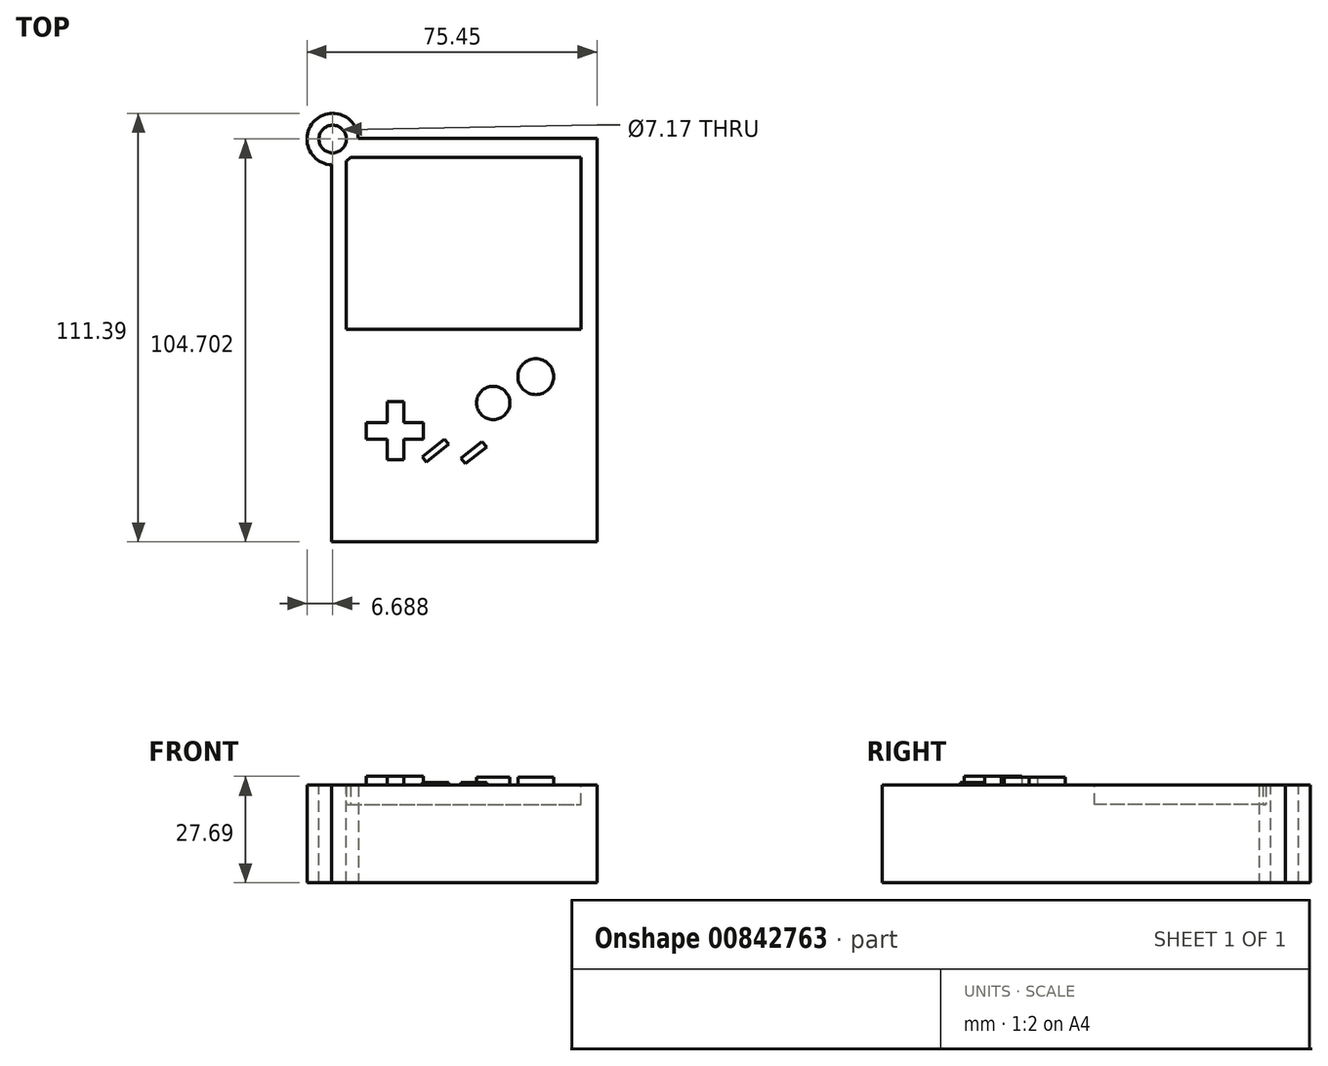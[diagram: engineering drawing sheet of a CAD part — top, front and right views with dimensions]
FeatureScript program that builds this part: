
annotation { "Feature Type Name" : "Feature", "Feature Type Description" : "" }
export const myFeature = defineFeature(function(context is Context, id is Id, definition is map)
    precondition{}
    {
        {
            var Q0;
            Q0=qCreatedBy(makeId("Top.planeOp"),FACE);
            var sketch = newSketch(context, id + "F0", { "sketchPlane" : qUnion([Q0])});
            skLineSegment(sketch, "E0.bottom", {"start": v(-34.82, 57.7) * mm, "end": v(34.25, 57.7) * mm});
            skLineSegment(sketch, "E0.top", {"start": v(-34.82, -47.18) * mm, "end": v(34.25, -47.18) * mm});
            skLineSegment(sketch, "E0.left", {"start": v(-34.82, 57.7) * mm, "end": v(-34.82, -47.18) * mm});
            skLineSegment(sketch, "E0.right", {"start": v(34.25, 57.7) * mm, "end": v(34.25, -47.18) * mm});
            skSolve(sketch);
        }
        {
            var Q0;
            Q0=makeQuery(id+"F0.imprint","IMPRINT",FACE,{"disambiguationData":[TD([[makeQuery(id+"F0.imprint","IMPRINT",EDGE,{"derivedFrom":sQuery(id+"F0.wireOp",EDGE,"E0.bottom")}),-1.0]])]});
            extrude(context, id + "F1", {"entities" : qUnion([Q0]), "depth" : 25.4 * mm, "offsetDistance" : 25.4 * mm});
        }
        {
            var Q0;
            Q0=makeQuery(id+"F1.opExtrude","CAP_FACE",FACE,{"disambiguationData":[OSD([sQuery(id+"F0.wireOp",EDGE,"E0.bottom"),sQuery(id+"F0.wireOp",EDGE,"E0.top"),sQuery(id+"F0.wireOp",EDGE,"E0.left"),sQuery(id+"F0.wireOp",EDGE,"E0.right")])],"isStart":false});
            var sketch = newSketch(context, id + "F2", { "sketchPlane" : qUnion([Q0])});
            skLineSegment(sketch, "E1.bottom", {"start": v(-30.93, 52.7) * mm, "end": v(30.15, 52.7) * mm});
            skLineSegment(sketch, "E1.top", {"start": v(-30.93, 8.02) * mm, "end": v(30.15, 8.02) * mm});
            skLineSegment(sketch, "E1.left", {"start": v(-30.93, 52.7) * mm, "end": v(-30.93, 8.02) * mm});
            skLineSegment(sketch, "E1.right", {"start": v(30.15, 52.7) * mm, "end": v(30.15, 8.02) * mm});
            skSolve(sketch);
        }
        {
            var Q0;
            Q0=makeQuery(id+"F2.imprint","IMPRINT",FACE,{"disambiguationData":[TD([[makeQuery(id+"F2.imprint","IMPRINT",EDGE,{"derivedFrom":sQuery(id+"F2.wireOp",EDGE,"E1.bottom")}),-1.0]])]});
            extrude(context, id + "F3", {"entities" : qUnion([Q0]), "operationType" : NewBodyOperationType.REMOVE, "oppositeDirection" : true, "depth" : 5.08 * mm, "offsetDistance" : 25.4 * mm});
        }
        {
            var Q0;
            Q0=makeQuery(id+"F1.opExtrude","CAP_FACE",FACE,{"disambiguationData":[OSD([sQuery(id+"F0.wireOp",EDGE,"E0.bottom"),sQuery(id+"F0.wireOp",EDGE,"E0.top"),sQuery(id+"F0.wireOp",EDGE,"E0.left"),sQuery(id+"F0.wireOp",EDGE,"E0.right")])],"isStart":false});
            var sketch = newSketch(context, id + "F4", { "sketchPlane" : qUnion([Q0])});
            skCircle(sketch, "E2", {"center": v(7.25, -11.08) * mm, "radius": 4.34 * mm});
            skCircle(sketch, "E3", {"center": v(18.33, -4.26) * mm, "radius": 4.66 * mm});
            skSolve(sketch);
        }
        {
            var Q0;
            Q0=qCreatedBy(makeId("Top.planeOp"),FACE);
            var sketch = newSketch(context, id + "F5", { "sketchPlane" : qUnion([Q0])});
            skCircle(sketch, "E4", {"center": v(-34.51, 57.52) * mm, "radius": 6.69 * mm});
            skSolve(sketch);
        }
        {
            var Q0;
            Q0=makeQuery(id+"F5.imprint","IMPRINT",FACE,{"disambiguationData":[TD([[makeQuery(id+"F5.imprint","IMPRINT",EDGE,{"derivedFrom":sQuery(id+"F5.wireOp",EDGE,"E4")}),1.0]])]});
            extrude(context, id + "F6", {"entities" : qUnion([Q0]), "operationType" : NewBodyOperationType.ADD, "depth" : 25.4 * mm, "offsetDistance" : 25.4 * mm});
        }
        {
            var Q0;
            Q0=makeQuery(id+"F6.boolean.opBoolean","MERGE",FACE,{"derivedFrom":[makeQuery(id+"F1.opExtrude","CAP_FACE",FACE,{"disambiguationData":[OSD([sQuery(id+"F0.wireOp",EDGE,"E0.bottom"),sQuery(id+"F0.wireOp",EDGE,"E0.top"),sQuery(id+"F0.wireOp",EDGE,"E0.left"),sQuery(id+"F0.wireOp",EDGE,"E0.right")])],"isStart":false}),makeQuery(id+"F6.opExtrude","CAP_FACE",FACE,{"disambiguationData":[OSD([sQuery(id+"F5.wireOp",EDGE,"E4")])],"isStart":false})]});
            var sketch = newSketch(context, id + "F7", { "sketchPlane" : qUnion([Q0])});
            skCircle(sketch, "E5", {"center": v(-34.51, 57.52) * mm, "radius": 3.58 * mm});
            skSolve(sketch);
        }
        {
            var Q0;
            Q0=makeQuery(id+"F7.imprint","IMPRINT",FACE,{"disambiguationData":[TD([[makeQuery(id+"F7.imprint","IMPRINT",EDGE,{"derivedFrom":sQuery(id+"F7.wireOp",EDGE,"E5")}),1.0]])]});
            extrude(context, id + "F8", {"entities" : qUnion([Q0]), "operationType" : NewBodyOperationType.REMOVE, "oppositeDirection" : true, "depth" : 25.4 * mm, "offsetDistance" : 25.4 * mm});
        }
        {
            var Q0;
            Q0=makeQuery(id+"F6.boolean.opBoolean","MERGE",FACE,{"derivedFrom":[makeQuery(id+"F1.opExtrude","CAP_FACE",FACE,{"disambiguationData":[OSD([sQuery(id+"F0.wireOp",EDGE,"E0.bottom"),sQuery(id+"F0.wireOp",EDGE,"E0.top"),sQuery(id+"F0.wireOp",EDGE,"E0.left"),sQuery(id+"F0.wireOp",EDGE,"E0.right")])],"isStart":false}),makeQuery(id+"F6.opExtrude","CAP_FACE",FACE,{"disambiguationData":[OSD([sQuery(id+"F5.wireOp",EDGE,"E4")])],"isStart":false})]});
            var sketch = newSketch(context, id + "F9", { "sketchPlane" : qUnion([Q0])});
            skLineSegment(sketch, "E6.bottom", {"start": v(-20.32, -25.86) * mm, "end": v(-16.06, -25.86) * mm});
            skLineSegment(sketch, "E6.top", {"start": v(-20.32, -10.8) * mm, "end": v(-16.06, -10.8) * mm});
            skLineSegment(sketch, "E6.left", {"start": v(-20.32, -25.86) * mm, "end": v(-20.32, -10.8) * mm});
            skLineSegment(sketch, "E6.right", {"start": v(-16.06, -25.86) * mm, "end": v(-16.06, -10.8) * mm});
            skLineSegment(sketch, "E7.bottom", {"start": v(-25.72, -16.2) * mm, "end": v(-10.94, -16.2) * mm});
            skLineSegment(sketch, "E7.top", {"start": v(-25.72, -20.46) * mm, "end": v(-10.94, -20.46) * mm});
            skLineSegment(sketch, "E7.left", {"start": v(-25.72, -16.2) * mm, "end": v(-25.72, -20.46) * mm});
            skLineSegment(sketch, "E7.right", {"start": v(-10.94, -16.2) * mm, "end": v(-10.94, -20.46) * mm});
            skSolve(sketch);
        }
        {
            var Q0;
            Q0 = qSketchRegion(id + "F9", true);
            extrude(context, id + "F10", {"entities" : qUnion([Q0]), "operationType" : NewBodyOperationType.ADD, "depth" : 2.3 * mm, "offsetDistance" : 25.4 * mm});
        }
        {
            var Q0;
            Q0 = qSketchRegion(id + "F4", true);
            extrude(context, id + "F11", {"entities" : qUnion([Q0]), "operationType" : NewBodyOperationType.ADD, "depth" : 2.03 * mm, "offsetDistance" : 25.4 * mm});
        }
        {
            var Q0;
            Q0=makeQuery(id+"F6.boolean.opBoolean","MERGE",FACE,{"derivedFrom":[makeQuery(id+"F1.opExtrude","CAP_FACE",FACE,{"disambiguationData":[OSD([sQuery(id+"F0.wireOp",EDGE,"E0.bottom"),sQuery(id+"F0.wireOp",EDGE,"E0.top"),sQuery(id+"F0.wireOp",EDGE,"E0.left"),sQuery(id+"F0.wireOp",EDGE,"E0.right")])],"isStart":false}),makeQuery(id+"F6.opExtrude","CAP_FACE",FACE,{"disambiguationData":[OSD([sQuery(id+"F5.wireOp",EDGE,"E4")])],"isStart":false})]});
            var sketch = newSketch(context, id + "F12", { "sketchPlane" : qUnion([Q0])});
            skLineSegment(sketch, "E8", {"start": v(4.32, -21.13) * mm, "end": v(5.63, -22.5) * mm});
            skLineSegment(sketch, "E9", {"start": v(5.63, -22.5) * mm, "end": v(0, -26.89) * mm});
            skLineSegment(sketch, "E10", {"start": v(0, -26.89) * mm, "end": v(-1.13, -25.44) * mm});
            skLineSegment(sketch, "E11", {"start": v(-1.13, -25.44) * mm, "end": v(4.32, -21.13) * mm});
            skSolve(sketch);
        }
        {
            var Q0;
            Q0=makeQuery(id+"F12.imprint","IMPRINT",FACE,{"disambiguationData":[TD([[makeQuery(id+"F12.imprint","IMPRINT",EDGE,{"derivedFrom":sQuery(id+"F12.wireOp",EDGE,"E8")}),1.0]])]});
            var sketch = newSketch(context, id + "F13", { "sketchPlane" : qUnion([Q0])});
            skLineSegment(sketch, "E12", {"start": v(-4.34, -21.8) * mm, "end": v(-10.1, -26.45) * mm});
            skLineSegment(sketch, "E13", {"start": v(-10.1, -26.45) * mm, "end": v(-11.14, -25.16) * mm});
            skLineSegment(sketch, "E14", {"start": v(-11.14, -25.16) * mm, "end": v(-5.47, -20.57) * mm});
            skLineSegment(sketch, "E15", {"start": v(-4.34, -21.8) * mm, "end": v(-5.47, -20.57) * mm});
            skSolve(sketch);
        }
        {
            var Q0;
            Q0 = qSketchRegion(id + "F12", true);
            var Q1;
            Q1 = qSketchRegion(id + "F13", true);
            extrude(context, id + "F14", {"entities" : qUnion([Q0, Q1]), "operationType" : NewBodyOperationType.ADD, "depth" : 0.63 * mm, "offsetDistance" : 25.4 * mm});
        }
    });
